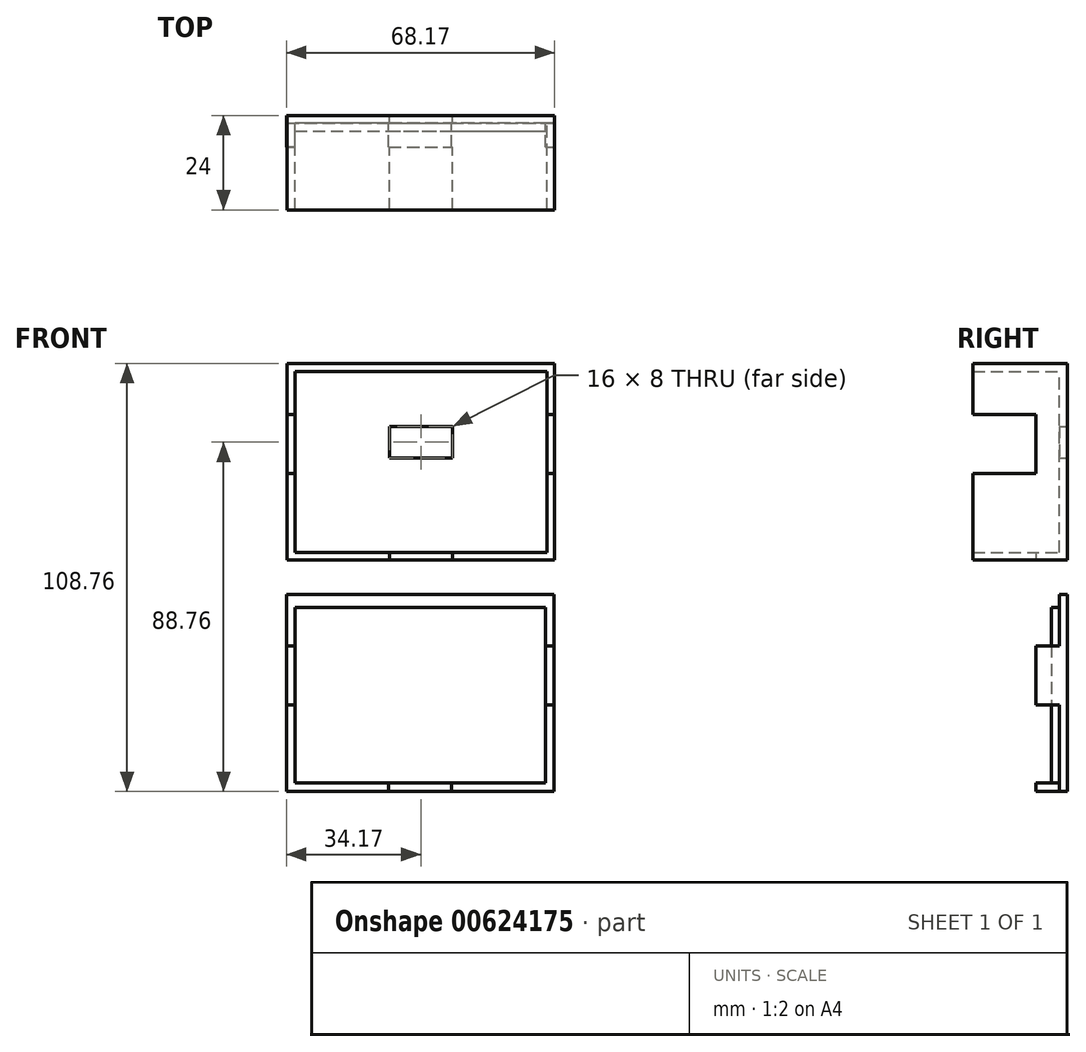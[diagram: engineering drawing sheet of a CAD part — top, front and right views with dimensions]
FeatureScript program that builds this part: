
annotation { "Feature Type Name" : "Feature", "Feature Type Description" : "" }
export const myFeature = defineFeature(function(context is Context, id is Id, definition is map)
    precondition{}
    {
        {
            var Q0;
            Q0=qCreatedBy(makeId("Front.planeOp"),FACE);
            var sketch = newSketch(context, id + "F0", { "sketchPlane" : qUnion([Q0])});
            skLineSegment(sketch, "E0.bottom", {"start": v(-34, 28) * mm, "end": v(34, 28) * mm});
            skLineSegment(sketch, "E0.top", {"start": v(-34, -22) * mm, "end": v(34, -22) * mm});
            skLineSegment(sketch, "E0.left", {"start": v(-34, 28) * mm, "end": v(-34, -22) * mm});
            skLineSegment(sketch, "E0.right", {"start": v(34, 28) * mm, "end": v(34, -22) * mm});
            skLineSegment(sketch, "E1.bottom", {"start": v(-32, 26) * mm, "end": v(32, 26) * mm});
            skLineSegment(sketch, "E1.top", {"start": v(-32, -20) * mm, "end": v(32, -20) * mm});
            skLineSegment(sketch, "E1.left", {"start": v(-32, 26) * mm, "end": v(-32, -20) * mm});
            skLineSegment(sketch, "E1.right", {"start": v(32, 26) * mm, "end": v(32, -20) * mm});
            skLineSegment(sketch, "E2", {"start": v(-8, -20) * mm, "end": v(-8, -22) * mm});
            skLineSegment(sketch, "E3", {"start": v(8, -20) * mm, "end": v(8, -22) * mm});
            skLineSegment(sketch, "E4.left", {"start": v(-8, 12) * mm, "end": v(-8, 4) * mm});
            skLineSegment(sketch, "E4.right", {"start": v(8, 12) * mm, "end": v(8, 4) * mm});
            skLineSegment(sketch, "E5.trimOffspring", {"start": v(-8, 12) * mm, "end": v(8, 12) * mm});
            skLineSegment(sketch, "E6.trimOffspring", {"start": v(-8, 4) * mm, "end": v(8, 4) * mm});
            skLineSegment(sketch, "E7", {"start": v(-34, 0) * mm, "end": v(-32, 0) * mm});
            skLineSegment(sketch, "E8.trimOffspring", {"start": v(32, 0) * mm, "end": v(34, 0) * mm});
            skLineSegment(sketch, "E9", {"start": v(-34, 15) * mm, "end": v(-32, 15) * mm});
            skLineSegment(sketch, "E10.trimOffspring", {"start": v(32, 15) * mm, "end": v(34, 15) * mm});
            skLineSegment(sketch, "E11.bottom", {"start": v(-34.17, -30.76) * mm, "end": v(33.83, -30.76) * mm});
            skLineSegment(sketch, "E11.top", {"start": v(-34.17, -80.76) * mm, "end": v(33.83, -80.76) * mm});
            skLineSegment(sketch, "E11.left", {"start": v(-34.17, -30.76) * mm, "end": v(-34.17, -80.76) * mm});
            skLineSegment(sketch, "E11.right", {"start": v(33.83, -30.76) * mm, "end": v(33.83, -80.76) * mm});
            skLineSegment(sketch, "E12.bottom", {"start": v(-31.97, -33.96) * mm, "end": v(31.63, -33.96) * mm});
            skLineSegment(sketch, "E12.top", {"start": v(-31.97, -78.56) * mm, "end": v(31.63, -78.56) * mm});
            skLineSegment(sketch, "E12.left", {"start": v(-31.97, -33.96) * mm, "end": v(-31.97, -78.56) * mm});
            skLineSegment(sketch, "E12.right", {"start": v(31.63, -33.96) * mm, "end": v(31.63, -78.56) * mm});
            skLineSegment(sketch, "E13", {"start": v(-31.97, -43.76) * mm, "end": v(-34.17, -43.76) * mm});
            skLineSegment(sketch, "E14", {"start": v(-34.17, -43.76) * mm, "end": v(-34.17, -58.76) * mm});
            skLineSegment(sketch, "E15", {"start": v(-34.17, -58.76) * mm, "end": v(-31.97, -58.76) * mm});
            skLineSegment(sketch, "E16", {"start": v(31.63, -43.76) * mm, "end": v(33.83, -43.76) * mm});
            skLineSegment(sketch, "E17", {"start": v(31.63, -58.76) * mm, "end": v(33.83, -58.76) * mm});
            skLineSegment(sketch, "E18", {"start": v(-8.17, -78.56) * mm, "end": v(-8.17, -80.76) * mm});
            skLineSegment(sketch, "E19", {"start": v(7.83, -78.56) * mm, "end": v(7.83, -80.76) * mm});
            skSolve(sketch);
        }
        {
            var Q0;
            {var subQ5=sQuery(id+"F0.wireOp",EDGE,"E1.bottom");Q0=makeQuery(id+"F0.imprint","IMPRINT",FACE,{"disambiguationData":[TD([[makeQuery(id+"F0.imprint","IMPRINT",EDGE,{"derivedFrom":subQ5}),-1.0]])]});}
            var Q1;
            {var subQ0=sQuery(id+"F0.wireOp",EDGE,"E8.trimOffspring");Q1=makeQuery(id+"F0.imprint","IMPRINT",FACE,{"disambiguationData":[TD([[makeQuery(id+"F0.imprint","IMPRINT",EDGE,{"derivedFrom":subQ0}),1.0]])]});}
            var Q2;
            {var subQ7=sQuery(id+"F0.wireOp",EDGE,"E3");Q2=makeQuery(id+"F0.imprint","IMPRINT",FACE,{"disambiguationData":[TD([[makeQuery(id+"F0.imprint","IMPRINT",EDGE,{"derivedFrom":subQ7}),1.0]])]});}
            var Q3;
            {var subQ1=sQuery(id+"F0.wireOp",EDGE,"E0.bottom");Q3=makeQuery(id+"F0.imprint","IMPRINT",FACE,{"disambiguationData":[TD([[makeQuery(id+"F0.imprint","IMPRINT",EDGE,{"derivedFrom":subQ1}),-1.0]])]});}
            var Q4;
            {var subQ0=sQuery(id+"F0.wireOp",EDGE,"E7");Q4=makeQuery(id+"F0.imprint","IMPRINT",FACE,{"disambiguationData":[TD([[makeQuery(id+"F0.imprint","IMPRINT",EDGE,{"derivedFrom":subQ0}),1.0]])]});}
            var Q5;
            {var subQ4=sQuery(id+"F0.wireOp",EDGE,"E2");Q5=makeQuery(id+"F0.imprint","IMPRINT",FACE,{"disambiguationData":[TD([[makeQuery(id+"F0.imprint","IMPRINT",EDGE,{"derivedFrom":subQ4}),-1.0]])]});}
            var Q6;
            {var subQ0=sQuery(id+"F0.wireOp",EDGE,"E2");Q6=makeQuery(id+"F0.imprint","IMPRINT",FACE,{"disambiguationData":[TD([[makeQuery(id+"F0.imprint","IMPRINT",EDGE,{"derivedFrom":subQ0}),1.0]])]});}
            extrude(context, id + "F1", {"entities" : qUnion([Q0, Q1, Q2, Q3, Q4, Q5, Q6]), "depth" : 2 * mm, "offsetDistance" : 25 * mm});
        }
        {
            var Q0;
            {var subQ0=sQuery(id+"F0.wireOp",EDGE,"E2");Q0=makeQuery(id+"F0.imprint","IMPRINT",FACE,{"disambiguationData":[TD([[makeQuery(id+"F0.imprint","IMPRINT",EDGE,{"derivedFrom":subQ0}),1.0]])]});}
            var Q1;
            {var subQ4=sQuery(id+"F0.wireOp",EDGE,"E2");Q1=makeQuery(id+"F0.imprint","IMPRINT",FACE,{"disambiguationData":[TD([[makeQuery(id+"F0.imprint","IMPRINT",EDGE,{"derivedFrom":subQ4}),-1.0]])]});}
            var Q2;
            {var subQ0=sQuery(id+"F0.wireOp",EDGE,"E7");Q2=makeQuery(id+"F0.imprint","IMPRINT",FACE,{"disambiguationData":[TD([[makeQuery(id+"F0.imprint","IMPRINT",EDGE,{"derivedFrom":subQ0}),1.0]])]});}
            var Q3;
            {var subQ7=sQuery(id+"F0.wireOp",EDGE,"E3");Q3=makeQuery(id+"F0.imprint","IMPRINT",FACE,{"disambiguationData":[TD([[makeQuery(id+"F0.imprint","IMPRINT",EDGE,{"derivedFrom":subQ7}),1.0]])]});}
            var Q4;
            {var subQ0=sQuery(id+"F0.wireOp",EDGE,"E8.trimOffspring");Q4=makeQuery(id+"F0.imprint","IMPRINT",FACE,{"disambiguationData":[TD([[makeQuery(id+"F0.imprint","IMPRINT",EDGE,{"derivedFrom":subQ0}),1.0]])]});}
            var Q5;
            {var subQ1=sQuery(id+"F0.wireOp",EDGE,"E0.bottom");Q5=makeQuery(id+"F0.imprint","IMPRINT",FACE,{"disambiguationData":[TD([[makeQuery(id+"F0.imprint","IMPRINT",EDGE,{"derivedFrom":subQ1}),-1.0]])]});}
            extrude(context, id + "F2", {"entities" : qUnion([Q0, Q1, Q2, Q3, Q4, Q5]), "operationType" : NewBodyOperationType.ADD, "depth" : 24 * mm, "offsetDistance" : 25 * mm});
        }
        {
            var Q0;
            {var subQ0=sQuery(id+"F0.wireOp",EDGE,"E7");Q0=makeQuery(id+"F0.imprint","IMPRINT",FACE,{"disambiguationData":[TD([[makeQuery(id+"F0.imprint","IMPRINT",EDGE,{"derivedFrom":subQ0}),1.0]])]});}
            var Q1;
            {var subQ0=sQuery(id+"F0.wireOp",EDGE,"E2");Q1=makeQuery(id+"F0.imprint","IMPRINT",FACE,{"disambiguationData":[TD([[makeQuery(id+"F0.imprint","IMPRINT",EDGE,{"derivedFrom":subQ0}),1.0]])]});}
            var Q2;
            {var subQ0=sQuery(id+"F0.wireOp",EDGE,"E8.trimOffspring");Q2=makeQuery(id+"F0.imprint","IMPRINT",FACE,{"disambiguationData":[TD([[makeQuery(id+"F0.imprint","IMPRINT",EDGE,{"derivedFrom":subQ0}),1.0]])]});}
            extrude(context, id + "F3", {"entities" : qUnion([Q0, Q1, Q2]), "operationType" : NewBodyOperationType.REMOVE, "depth" : 24 * mm, "offsetDistance" : 25 * mm, "hasSecondDirection" : true, "secondDirectionOppositeDirection" : false, "secondDirectionDepth" : 8 * mm});
        }
        {
            var Q0;
            Q0=makeQuery(id+"F0.imprint","IMPRINT",FACE,{"disambiguationData":[TD([[makeQuery(id+"F0.imprint","IMPRINT",EDGE,{"derivedFrom":sQuery(id+"F0.wireOp",EDGE,"E12.bottom")}),-1.0]])]});
            var Q1;
            Q1=makeQuery(id+"F0.imprint","IMPRINT",FACE,{"disambiguationData":[TD([[makeQuery(id+"F0.imprint","IMPRINT",EDGE,{"derivedFrom":sQuery(id+"F0.wireOp",EDGE,"E11.bottom")}),-1.0]])]});
            var Q2;
            {var subQ0=sQuery(id+"F0.wireOp",EDGE,"E13");Q2=makeQuery(id+"F0.imprint","IMPRINT",FACE,{"disambiguationData":[TD([[makeQuery(id+"F0.imprint","IMPRINT",EDGE,{"derivedFrom":subQ0}),1.0]])]});}
            var Q3;
            {var subQ3=sQuery(id+"F0.wireOp",EDGE,"E15");Q3=makeQuery(id+"F0.imprint","IMPRINT",FACE,{"disambiguationData":[TD([[makeQuery(id+"F0.imprint","IMPRINT",EDGE,{"derivedFrom":subQ3}),-1.0]])]});}
            var Q4;
            {var subQ0=sQuery(id+"F0.wireOp",EDGE,"E18");Q4=makeQuery(id+"F0.imprint","IMPRINT",FACE,{"disambiguationData":[TD([[makeQuery(id+"F0.imprint","IMPRINT",EDGE,{"derivedFrom":subQ0}),1.0]])]});}
            var Q5;
            {var subQ4=sQuery(id+"F0.wireOp",EDGE,"E17");Q5=makeQuery(id+"F0.imprint","IMPRINT",FACE,{"disambiguationData":[TD([[makeQuery(id+"F0.imprint","IMPRINT",EDGE,{"derivedFrom":subQ4}),-1.0]])]});}
            var Q6;
            {var subQ0=sQuery(id+"F0.wireOp",EDGE,"E16");Q6=makeQuery(id+"F0.imprint","IMPRINT",FACE,{"disambiguationData":[TD([[makeQuery(id+"F0.imprint","IMPRINT",EDGE,{"derivedFrom":subQ0}),-1.0]])]});}
            extrude(context, id + "F4", {"entities" : qUnion([Q0, Q1, Q2, Q3, Q4, Q5, Q6]), "depth" : 2 * mm, "offsetDistance" : 25 * mm});
        }
        {
            var Q0;
            Q0=makeQuery(id+"F0.imprint","IMPRINT",FACE,{"disambiguationData":[TD([[makeQuery(id+"F0.imprint","IMPRINT",EDGE,{"derivedFrom":sQuery(id+"F0.wireOp",EDGE,"E12.bottom")}),-1.0]])]});
            extrude(context, id + "F5", {"entities" : qUnion([Q0]), "operationType" : NewBodyOperationType.ADD, "depth" : 4 * mm, "offsetDistance" : 25 * mm});
        }
        {
            var Q0;
            {var subQ0=sQuery(id+"F0.wireOp",EDGE,"E13");Q0=makeQuery(id+"F0.imprint","IMPRINT",FACE,{"disambiguationData":[TD([[makeQuery(id+"F0.imprint","IMPRINT",EDGE,{"derivedFrom":subQ0}),1.0]])]});}
            var Q1;
            {var subQ0=sQuery(id+"F0.wireOp",EDGE,"E18");Q1=makeQuery(id+"F0.imprint","IMPRINT",FACE,{"disambiguationData":[TD([[makeQuery(id+"F0.imprint","IMPRINT",EDGE,{"derivedFrom":subQ0}),1.0]])]});}
            var Q2;
            {var subQ0=sQuery(id+"F0.wireOp",EDGE,"E16");Q2=makeQuery(id+"F0.imprint","IMPRINT",FACE,{"disambiguationData":[TD([[makeQuery(id+"F0.imprint","IMPRINT",EDGE,{"derivedFrom":subQ0}),-1.0]])]});}
            extrude(context, id + "F6", {"entities" : qUnion([Q0, Q1, Q2]), "operationType" : NewBodyOperationType.ADD, "depth" : 8 * mm, "offsetDistance" : 25 * mm});
        }
    });
